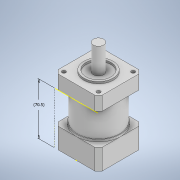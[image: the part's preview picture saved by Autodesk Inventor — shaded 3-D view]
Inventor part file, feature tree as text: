
AUTODESK INVENTOR PART (.ipt)
format: ipt  version: 2021 (Build 250183000, 183)  size: 198,144 bytes
history: native  units: mm
features: sketch x8, extrude x7, chamfer x1
ambient origin geometry x8: Origin, YZ Plane, XZ Plane, XY Plane, X Axis, Y Axis, Z Axis, Center Point
bodies: Solid1 (feature_tree)
feature tree (16):
  extrude  "Extrusion1"  Depth=60.0mm
  extrude  "Extrusion2"  Depth=28.0mm TaperAngle=0.0deg
  extrude  "Extrusion3"  Depth=3.0mm
  sketch  "Sketch4"  dims[d8=39.5mm d9=0.0mm d10=5.0mm]
  sketch  "Sketch5"  dims[d11=5.0mm d12=47.15mm d13=5.0mm]
  extrude  "Extrusion4"  Depth=39.5mm
  extrude  "Extrusion5"  Depth=5.0mm
  extrude  "Extrusion6"  Depth=47.15mm
  chamfer  "Chamfer1"  Distance=19.0mm
  extrude  "Extrusion7"  Depth=70.5mm
  sketch  "Sketch1"  dims[d0=60.0mm d1=60.0mm]
  sketch  "Sketch2"  dims[d2=58.0mm d3=28.0mm d4=0.0mm]
  sketch  "Sketch3"  dims[d5=3.0mm d6=0.0mm d7=58.0mm]
  sketch  "Sketch6"  dims[d14=5.0mm d15=47.15mm d16=47.15mm]
  sketch  "Sketch7"  dims[d17=47.15mm d18=69.500001mm d19=19.0mm]
  sketch  "Sketch8"  dims[d20=0.0mm d21=70.5mm d22=14.0mm d23=40.0mm d24=3.0mm d25=2.5mm d26=0.0mm d27=14.0mm d28=35.0mm d29=0.0mm d30=5.0mm d31=2.0mm d32=45.0deg d33=8.0mm d34=30.0mm d35=0.0mm]
